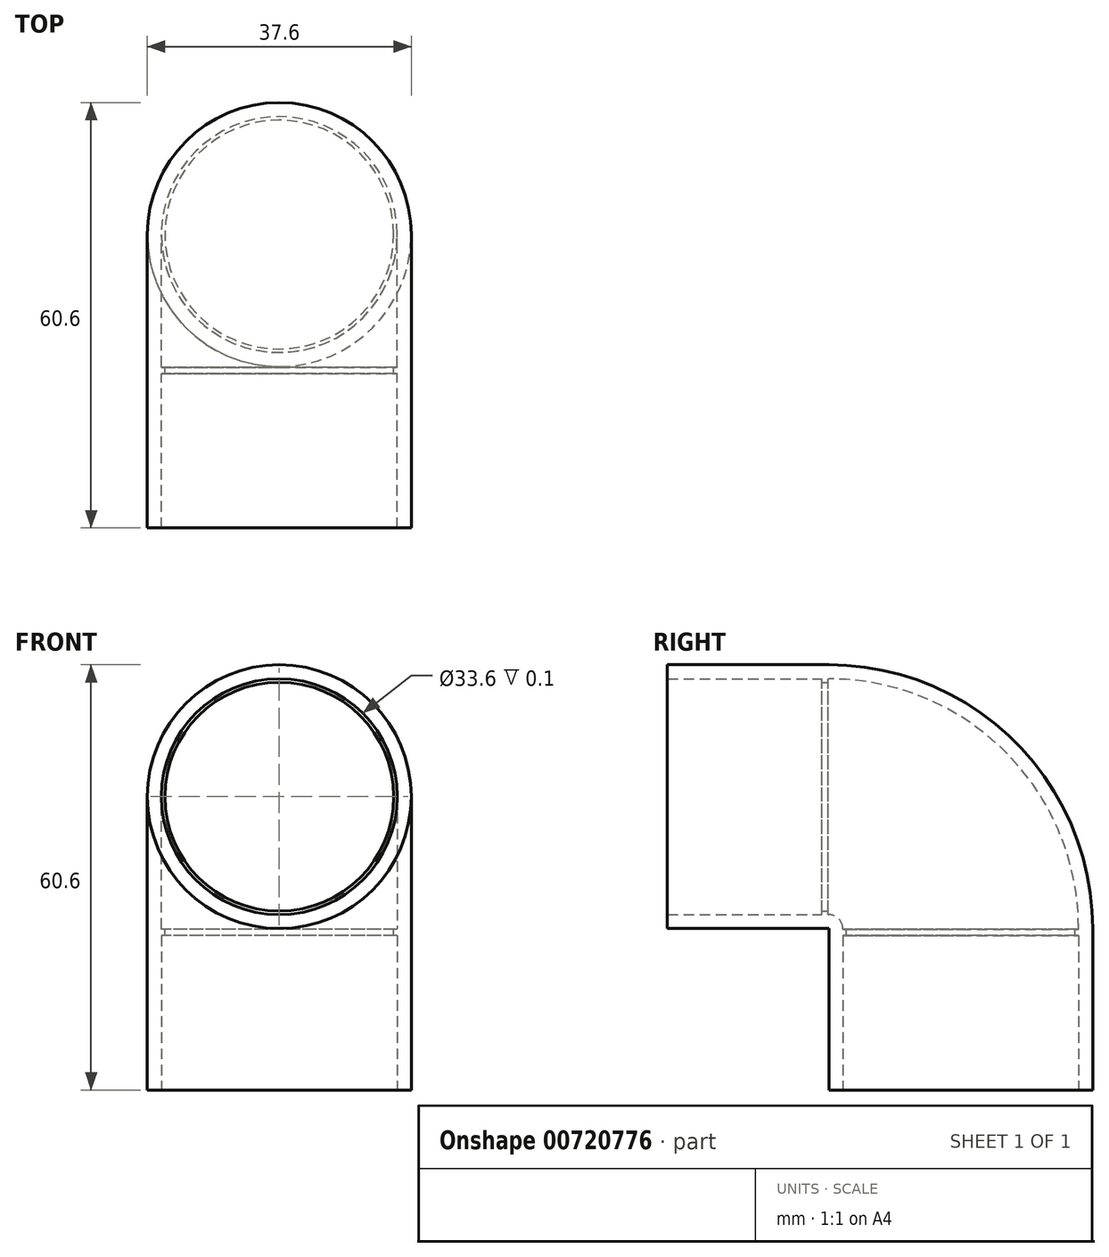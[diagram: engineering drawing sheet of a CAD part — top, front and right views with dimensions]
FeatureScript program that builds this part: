
annotation { "Feature Type Name" : "Feature", "Feature Type Description" : "" }
export const myFeature = defineFeature(function(context is Context, id is Id, definition is map)
    precondition{}
    {
        {
            var Q0;
            Q0=qCreatedBy(makeId("Top.planeOp"),FACE);
            var sketch = newSketch(context, id + "F0", { "sketchPlane" : qUnion([Q0])});
            skCircle(sketch, "E0", {"center": v(0, 0) * mm, "radius": 16.8 * mm});
            skCircle(sketch, "E1", {"center": v(0, 0) * mm, "radius": 16.3 * mm});
            skCircle(sketch, "E2", {"center": v(0, 0) * mm, "radius": 18.8 * mm});
            skSolve(sketch);
        }
        {
            var Q0;
            Q0 = qSketchRegion(id + "F0", true);
            extrude(context, id + "F1", {"entities" : qUnion([Q0]), "depth" : 23 * mm, "offsetDistance" : 25 * mm});
        }
        {
            var Q0;
            Q0=makeQuery(id+"F1.opExtrude","CAP_FACE",FACE,{"disambiguationData":[OSD([sQuery(id+"F0.wireOp",EDGE,"E0"),sQuery(id+"F0.wireOp",EDGE,"E2")])],"isStart":false});
            var sketch = newSketch(context, id + "F2", { "sketchPlane" : qUnion([Q0])});
            skCircle(sketch, "E3", {"center": v(0, 0) * mm, "radius": 16.8 * mm});
            skCircle(sketch, "E4", {"center": v(0, 0) * mm, "radius": 16.3 * mm});
            skSolve(sketch);
        }
        {
            var Q0;
            Q0=makeQuery(id+"F2.imprint","IMPRINT",FACE,{"disambiguationData":[TD([[makeQuery(id+"F2.imprint","IMPRINT",EDGE,{"derivedFrom":sQuery(id+"F2.wireOp",EDGE,"E3")}),1.0]])]});
            extrude(context, id + "F3", {"entities" : qUnion([Q0]), "operationType" : NewBodyOperationType.ADD, "oppositeDirection" : true, "depth" : 1 * mm, "offsetDistance" : 25 * mm});
        }
        {
            var Q0;
            Q0=qCreatedBy(makeId("Front.planeOp"),FACE);
            cPlane(context, id + "F4", {"entities" : qUnion([Q0]), "cplaneType" : CPlaneType.OFFSET, "offset" : 18.8 * mm, "width" : 150 * mm, "height" : 150 * mm});
        }
        {
            var Q0;
            Q0=qCreatedBy(id+"F4.planeOp",FACE);
            var sketch = newSketch(context, id + "F5", { "sketchPlane" : qUnion([Q0])});
            skLineSegment(sketch, "E5", {"start": v(0, 0) * mm, "end": v(0, 23) * mm, "construction": true});
            skLineSegment(sketch, "E6", {"start": v(0, 23) * mm, "end": v(0, 41.8) * mm, "construction": true});
            skCircle(sketch, "E7", {"center": v(0, 41.8) * mm, "radius": 18.8 * mm});
            skCircle(sketch, "E8", {"center": v(0, 41.8) * mm, "radius": 16.8 * mm});
            skCircle(sketch, "E9", {"center": v(0, 41.8) * mm, "radius": 16.3 * mm});
            skSolve(sketch);
        }
        {
            var Q0;
            Q0=makeQuery(id+"F5.imprint","IMPRINT",FACE,{"disambiguationData":[TD([[makeQuery(id+"F5.imprint","IMPRINT",EDGE,{"derivedFrom":sQuery(id+"F5.wireOp",EDGE,"E7")}),1.0]])]});
            extrude(context, id + "F6", {"entities" : qUnion([Q0]), "operationType" : NewBodyOperationType.ADD, "depth" : 23 * mm, "offsetDistance" : 25 * mm});
        }
        {
            var Q0;
            Q0=makeQuery(id+"F5.imprint","IMPRINT",FACE,{"disambiguationData":[TD([[makeQuery(id+"F5.imprint","IMPRINT",EDGE,{"derivedFrom":sQuery(id+"F5.wireOp",EDGE,"E8")}),1.0]])]});
            extrude(context, id + "F7", {"entities" : qUnion([Q0]), "operationType" : NewBodyOperationType.ADD, "depth" : 1 * mm, "offsetDistance" : 25 * mm});
        }
        {
            var Q0;
            Q0=makeQuery(id+"F5.imprint","IMPRINT",FACE,{"disambiguationData":[TD([[makeQuery(id+"F5.imprint","IMPRINT",EDGE,{"derivedFrom":sQuery(id+"F5.wireOp",EDGE,"E8")}),1.0]])]});
            extrude(context, id + "F8", {"entities" : qUnion([Q0]), "operationType" : NewBodyOperationType.REMOVE, "depth" : .1 * mm, "offsetDistance" : 25 * mm});
        }
        {
            var Q0;
            Q0=makeQuery(id+"F2.imprint","IMPRINT",FACE,{"disambiguationData":[TD([[makeQuery(id+"F2.imprint","IMPRINT",EDGE,{"derivedFrom":sQuery(id+"F2.wireOp",EDGE,"E3")}),1.0]])]});
            extrude(context, id + "F9", {"entities" : qUnion([Q0]), "operationType" : NewBodyOperationType.REMOVE, "oppositeDirection" : true, "depth" : .1 * mm, "offsetDistance" : 25 * mm});
        }
        {
            var Q0;
            Q0=qCreatedBy(makeId("Right.planeOp"),FACE);
            var sketch = newSketch(context, id + "F10", { "sketchPlane" : qUnion([Q0])});
            skLineSegment(sketch, "E10", {"start": v(0, 0) * mm, "end": v(0, 23) * mm, "construction": true});
            skLineSegment(sketch, "E11", {"start": v(0, 23) * mm, "end": v(-18.8, 23) * mm, "construction": true});
            skLineSegment(sketch, "E12", {"start": v(0, 23) * mm, "end": v(18.8, 23) * mm, "construction": true});
            skArc(sketch, "E13", {"start": v(18.8, 23) * mm, "mid": v(7.79, 49.59) * mm, "end": v(-18.8, 60.6) * mm});
            skSolve(sketch);
        }
        {
            var Q0;
            {var subQ0=sQuery(id+"F5.wireOp",EDGE,"E8");Q0=makeQuery(id+"F7.boolean.opBoolean","MERGE",FACE,{"derivedFrom":[makeQuery(id+"F6.opExtrude","CAP_FACE",FACE,{"disambiguationData":[OSD([sQuery(id+"F5.wireOp",EDGE,"E7"),subQ0])],"isStart":true}),makeQuery(id+"F7.opExtrude","CAP_FACE",FACE,{"disambiguationData":[OSD([subQ0,sQuery(id+"F5.wireOp",EDGE,"E9")])],"isStart":true})]});}
            var Q1;
            Q1=makeQuery(id+"F3.boolean.opBoolean","MERGE",FACE,{"derivedFrom":[makeQuery(id+"F1.opExtrude","CAP_FACE",FACE,{"disambiguationData":[OSD([sQuery(id+"F0.wireOp",EDGE,"E0"),sQuery(id+"F0.wireOp",EDGE,"E2")])],"isStart":false}),makeQuery(id+"F3.opExtrude","CAP_FACE",FACE,{"disambiguationData":[OSD([sQuery(id+"F2.wireOp",EDGE,"E3"),sQuery(id+"F2.wireOp",EDGE,"E4")])],"isStart":true})]});
            var Q2;
            Q2=sQuery(id+"F10.wireOp",EDGE,"E13");
            sweep(context, id + "F11", {"operationType" : NewBodyOperationType.ADD, "profiles" : qUnion([Q0, Q1]), "path" : qUnion([Q2])});
        }
    });
